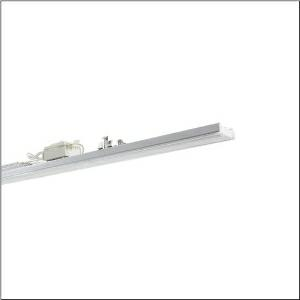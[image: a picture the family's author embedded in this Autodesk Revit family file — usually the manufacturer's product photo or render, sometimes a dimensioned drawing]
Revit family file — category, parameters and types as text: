
# Revit family: licross_r__11_recessed_mo_51te11dv4fxg_01a2
name_source: partatom
category: Lighting Fixtures
units: mm (PartAtom-declared; Revit-internal decimal feet)

## family parameters
Cut with Voids When Loaded = No
Host = Face
Light Source = No
Part Type = Normal
Room Calculation Point = No
Round Connector Dimension = Use Diameter
Shared = No

## types (1)
- --- (1 x LED, 15120 lm, 84.1 W, 4000K)
    Apparent Load = 84 VA
    CIE Flux Codes = 89 96 99 100 100
    Color Rendering = 80
    Color Temperature = 4000K
    Default Elevation = 1800 mm
    Description = Licross® 11 Recessed MO, luminaire insert, of sheet steel, galvanised, coil coated, white, length: 2.250mm, width: 66mm, height: 67mm, LED rated luminous flux: 15.120lm, light colour: 840, control gear: DALI 2, with plug, 5-pole, with phase selection, mains connection: 220..240V, AC, 50/60Hz, rated input power: 84W, halogen-free wiring, primary light control with lens, of plastic, primary optical cover: cover, of PMMA, light emission: direct distribution, primary light characteristic: symmetric, protection rating (complete): IP54, insulation class (complete): insulation class I (protective earthing), certification: CE, ENEC, VDE, UKCA, protection symbol: D if used in an environment with non-conductive dust loads with corresponding accessories, impact resistance: IK06, permissible ambient temperature for indoor applications: -25..+35°C, corresponds to IFS (International Featured Standards) requirements for safety and quality in the food industry, reducing of maximum allowable ambient temperature of 5°C with ceiling mounting, LABS conformity tested according to VDMA 24364:2018-05, packaging unit: 1 piece
    Height = 58 mm
    Lamp = 1 x LED
    Lamp Light Flux = 15120 lm
    Lamp Power = 84.1 W
    Lamp count = 1
    Length = 2250 mm
    Luminous efficacy = 180 lm/W
    Manufacturer = Siteco
    ModVariant = No
    Model = 51TE11DV4FXG
    Mounting Place = Ceiling
    Mounting Type = Pendant
    Number of Poles = 1
    OnlyDefault = Yes
    Power Factor = 1
    Product Name = Licross® 11 Recessed MO
    Product group = luminaire insert
    ProductGroupID = 901
    Protection Class = Protection class I
    Protection Degree = IP 54
    RLX_Detail_Level = 1
    RLX_Emergency_Light_Flux = 0 lm
    RLX_Emergency_Type = 0
    RLX_Emergency_Type_DB = No
    RlxData = <blob elided: 29401 chars, md5=e8551027>
    Socket = socket
    Standby Power = 0 W
    System Light Flux = 15120 lm
    System Power = 84 W
    Type Comments = factory setting: luminous flux: 100 % | dim-lin: 254 | 378 mA
    Type Image = l_1296930.jpg
    URL = http://relux.com
    VarID = @adj_096010
    Voltage = 0 V
    Weight = 0.00 kg
    Width = 66 mm

## geometry (parser evidence)
native form markers: Blend x4, Sweep x10
no freeform markers — native parametric forms only
